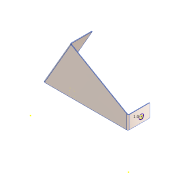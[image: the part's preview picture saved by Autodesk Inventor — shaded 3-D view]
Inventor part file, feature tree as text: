
AUTODESK INVENTOR PART (.ipt)
format: ipt  version: 2016 (Build 200138000, 138)  size: 201,216 bytes
history: native  units: in
note: dims shown in document units (in); Inventor stores cm internally (conversion verified against a paired STEP export)
features: reference x11, sheet_metal_op x7, sketch x6, other x6, fillet x1
ambient origin geometry x8: Origin, YZ Plane, XZ Plane, XY Plane, X Axis, Y Axis, Z Axis, Center Point
bodies: Solid1 (feature_tree)
feature tree (31):
  sheet_metal_op  "Face1"
  sheet_metal_op  "Flange1"
  sketch  "Sketch5"  dims[d8=3.0in]
  sheet_metal_op  "Flange2"
  fillet  "Fillet1"  Radius=30.0in
  sketch  "Sketch7"  dims[d10=90.0deg d11=13.0167in d12=0.125in d13=0.0in d14=0.125in d15=0.0625in d16=0.25in d17=0.125in d18=5.0in d19=90.0deg d20=0.125in d21=0.5in d22=0.125in d23=0.125in d24=0.125in d25=0.0625in d26=0.25in d27=0.125in d28=5.0in d29=90.0deg d30=0.125in d31=0.5in d32=0.125in d33=0.125in d36=1.063in d37=0.125in d38=0.0in d39=0.125in]
  sketch  "Sketch1"  dims[d1=30.0in]
  other  "Plate1"
  sketch  "Sketch3"  dims[d2=0.125in]
  reference  "Reference12"
  reference  "Reference13"
  reference  "Reference14"
  sketch  "Sketch4"  dims[d7=60.0deg]
  other  "Plate2"
  sheet_metal_op  "Bend1"
  sheet_metal_op  "Corner1"
  reference  "Reference15"
  reference  "Reference16"
  reference  "Reference17"
  sketch  "Sketch6"  dims[d9=180.0deg]
  other  "Plate3"
  sheet_metal_op  "Bend2"
  sheet_metal_op  "Corner2"
  reference  "Reference18"
  reference  "Reference19"
  reference  "Reference20"
  reference  "Reference21"
  reference  "Reference22"
  other  "Cut1"
  other  "Cut2"
  other  "Definition1"
